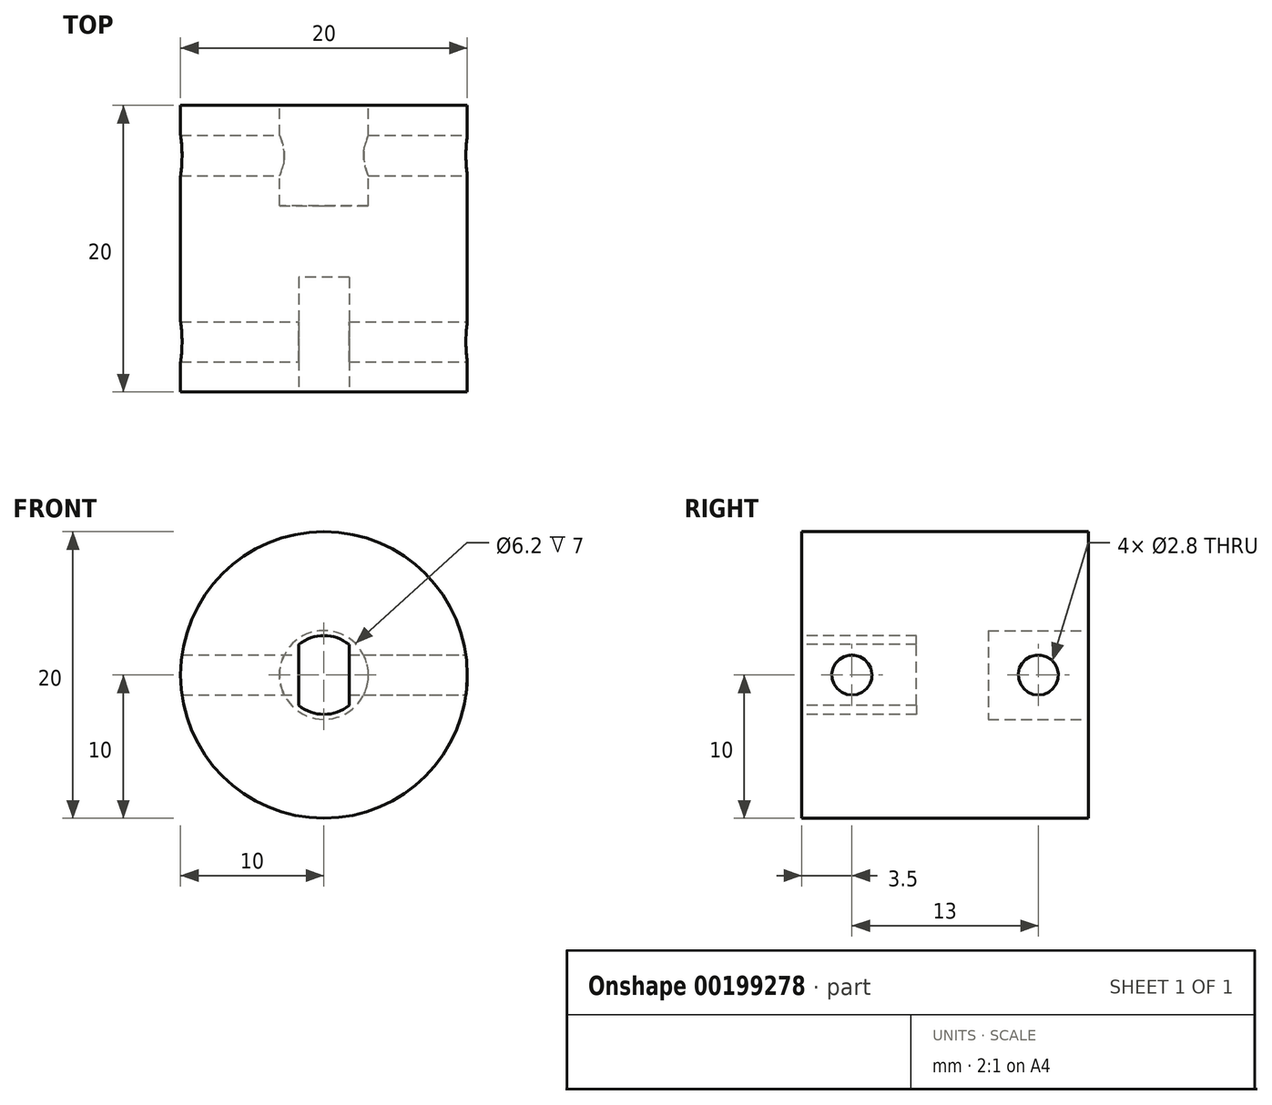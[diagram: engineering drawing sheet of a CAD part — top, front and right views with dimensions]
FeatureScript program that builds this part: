
annotation { "Feature Type Name" : "Feature", "Feature Type Description" : "" }
export const myFeature = defineFeature(function(context is Context, id is Id, definition is map)
    precondition{}
    {
        {
            var Q0;
            Q0=qCreatedBy(makeId("Front.planeOp"),FACE);
            var sketch = newSketch(context, id + "F0", { "sketchPlane" : qUnion([Q0])});
            skCircle(sketch, "E0", {"center": v(0, 0) * mm, "radius": 10 * mm});
            skSolve(sketch);
        }
        {
            var Q0;
            Q0=qSketchRegion(id+"F0",true);
            extrude(context, id + "F1", {"entities" : qUnion([Q0]), "depth" : 20 * mm});
        }
        {
            var Q0;
            Q0=makeQuery(id+"F1.opExtrude","CAP_FACE",FACE,{"disambiguationData":[OSD([sQuery(id+"F0.wireOp",EDGE,"E0")])],"isStart":false});
            var sketch = newSketch(context, id + "F2", { "sketchPlane" : qUnion([Q0])});
            skArc(sketch, "E1", {"start": v(1.75, 2.12) * mm, "mid": v(0, 2.75) * mm, "end": v(-1.75, 2.12) * mm});
            skLineSegment(sketch, "E2.left", {"start": v(-1.75, -2.12) * mm, "end": v(-1.75, 2.12) * mm});
            skLineSegment(sketch, "E2.right", {"start": v(1.75, -2.12) * mm, "end": v(1.75, 2.12) * mm});
            skArc(sketch, "E3.trimOffspring", {"start": v(-1.75, -2.12) * mm, "mid": v(0, -2.75) * mm, "end": v(1.75, -2.12) * mm});
            skSolve(sketch);
        }
        {
            var Q0;
            Q0=qSketchRegion(id+"F2",true);
            extrude(context, id + "F3", {"entities" : qUnion([Q0]), "operationType" : NewBodyOperationType.REMOVE, "oppositeDirection" : true, "depth" : 8 * mm});
        }
        {
            var Q0;
            Q0=makeQuery(id+"F1.opExtrude","CAP_FACE",FACE,{"disambiguationData":[OSD([sQuery(id+"F0.wireOp",EDGE,"E0")])],"isStart":true});
            var sketch = newSketch(context, id + "F4", { "sketchPlane" : qUnion([Q0])});
            skCircle(sketch, "E4", {"center": v(0, 0) * mm, "radius": 3.1 * mm});
            skSolve(sketch);
        }
        {
            var Q0;
            Q0=qSketchRegion(id+"F4",true);
            extrude(context, id + "F5", {"entities" : qUnion([Q0]), "operationType" : NewBodyOperationType.REMOVE, "oppositeDirection" : true, "depth" : 7 * mm});
        }
        {
            var Q0;
            Q0=qCreatedBy(makeId("Right.planeOp"),FACE);
            var sketch = newSketch(context, id + "F6", { "sketchPlane" : qUnion([Q0])});
            skCircle(sketch, "E5", {"center": v(-3.5, 0) * mm, "radius": 1.4 * mm});
            skLineSegment(sketch, "E6", {"start": v(0, 0) * mm, "end": v(-20, 0) * mm, "construction": true});
            skLineSegment(sketch, "E7", {"start": v(-10, 0) * mm, "end": v(-10, 9.98) * mm, "construction": true});
            skCircle(sketch, "E8.MirrorC", {"center": v(-16.5, 0) * mm, "radius": 1.4 * mm});
            skSolve(sketch);
        }
        {
            var Q0;
            Q0=qSketchRegion(id+"F6",true);
            extrude(context, id + "F7", {"entities" : qUnion([Q0]), "operationType" : NewBodyOperationType.REMOVE, "endBound" : BoundingType.SYMMETRIC, "oppositeDirection" : true, "depth" : 25 * mm});
        }
    });
